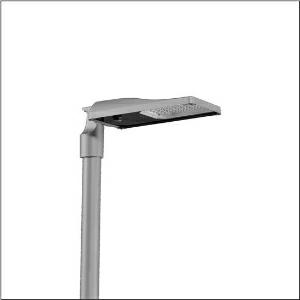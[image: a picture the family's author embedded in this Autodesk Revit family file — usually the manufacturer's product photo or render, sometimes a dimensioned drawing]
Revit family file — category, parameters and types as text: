
# Revit family: streetlight_sl_31_mini___st1_0a_5xh6d31r08ha_6f87
name_source: partatom
category: Lighting Fixtures
units: mm (PartAtom-declared; Revit-internal decimal feet)

## family parameters
Cut with Voids When Loaded = No
Host = Face
Light Source = No
Part Type = Normal
Room Calculation Point = No
Round Connector Dimension = Use Diameter
Shared = No

## types (1)
- --- (1 x LED, 9230 lm, 68.3 W, 3000K)
    Apparent Load = 68 VA
    CIE Flux Codes = 37 72 97 100 100
    Color Rendering = 70
    Color Temperature = 3000K
    Default Elevation = 1800 mm
    Description = Streetlight SL 31 mini D4i, Desk-Remote mast luminaire for post-top, side-entry; light control with lens of PMMA; light distribution: ST1.0a, direct asymmetric distribution, for standard-compliant lighting for roads and squares; LED: luminous flux: 9.230lm, light colour: 730, colour temperature: 3000K; luminous efficacy: 135,1lm/W; control: pre-setting: logarithmic dimming characteristic, flexible luminous flux parameterisation, time-dependent luminous flux control, constant luminous flux control, power reduction, intelligent temperature release in ECG and LED module, overheat protection; luminaire housing, of diecast aluminium, SITECO metallic grey (DB 702S), corrosivity category C5 high according to DIN EN ISO 12944; cover of toughened safety glass, transparent, opened without tools; mast flange of diecast aluminium, SITECO metallic grey (DB 702S), spigot size: 76/60mm, mast flange included unmounted; with cable H07RN-F 2x 1.5mm², cable length: 8,5m, connection cable pre-assembled; mains connection: 220..240V, AC, 50/60Hz; power consumption (at start of service life): 68,3W / (at end of service life): 74,5W / (with reduced operation 50%): 29,5W; protection rating (complete): IP66; insulation class (complete): insulation class II (safety insulation); impact resistance: IK09; certification: CE, ENEC, ENEC+, VDE, UKCA, ZD4i; permissible operating ambient temperature for outdoor applications: -40..+50°C; packaging unit: 1 piece

Light Distribution: ST1.0a
    Height = 76 mm
    Lamp = 1 x LED
    Lamp Light Flux = 9230 lm
    Lamp Power = 68.3 W
    Lamp count = 1
    Length = 547 mm
    Luminous efficacy = 135 lm/W
    Manufacturer = Siteco
    ModVariant = No
    Model = 5XH6D31R08HA
    Number of Poles = 1
    OnlyDefault = Yes
    Power Factor = 1
    Product Name = Streetlight SL 31 mini | ST1.0a
    Product group = mast luminaire | pylon top
    ProductGroupID = 6100
    Protection Class = Protection class II
    Protection Degree = IP 66
    RLX_Detail_Level = 1
    RLX_Emergency_Light_Flux = 0 lm
    RLX_Emergency_Type = 0
    RLX_Emergency_Type_DB = No
    RlxData = <blob elided: 24285 chars, md5=90b4ef1c>
    Socket = socket
    Standby Power = 0 W
    System Light Flux = 9230 lm
    System Power = 68 W
    Type Comments = factory setting: luminous flux: 100 % | dim-lin: 254 | 692 mA
    Type Image = l_1300328.jpg
    URL = http://relux.com
    VarID = @adj_020435
    Voltage = 0 V
    Weight = 0.00 kg
    Width = 265 mm

## geometry (parser evidence)
native form markers: Blend x4, Sweep x11
no freeform markers — native parametric forms only
